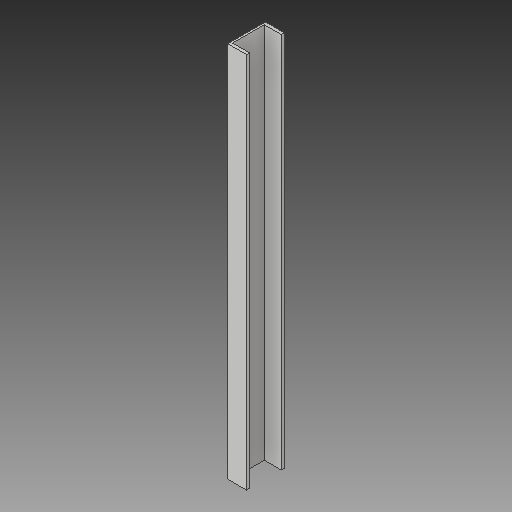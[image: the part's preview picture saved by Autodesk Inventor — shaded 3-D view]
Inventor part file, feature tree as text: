
AUTODESK INVENTOR PART (.ipt)
format: ipt  version: 2019 (Build 230136000, 136)  size: 87,040 bytes
history: native  units: in
note: dims shown in document units (in); Inventor stores cm internally (conversion verified against a paired STEP export)
features: other x3, sketch x1
ambient origin geometry x8: Origin, YZ Plane, XZ Plane, XY Plane, X Axis, Y Axis, Z Axis, Center Point
bodies: Solid1 (feature_tree)
feature tree (4):
  other  "Channel1_MIR5.ipt"
  other  "Solid1::Channel1_MIR5.ipt"
  other  "TaggingFeature1"
  sketch  "Sketch1"  dims[d0=0.3937in]
